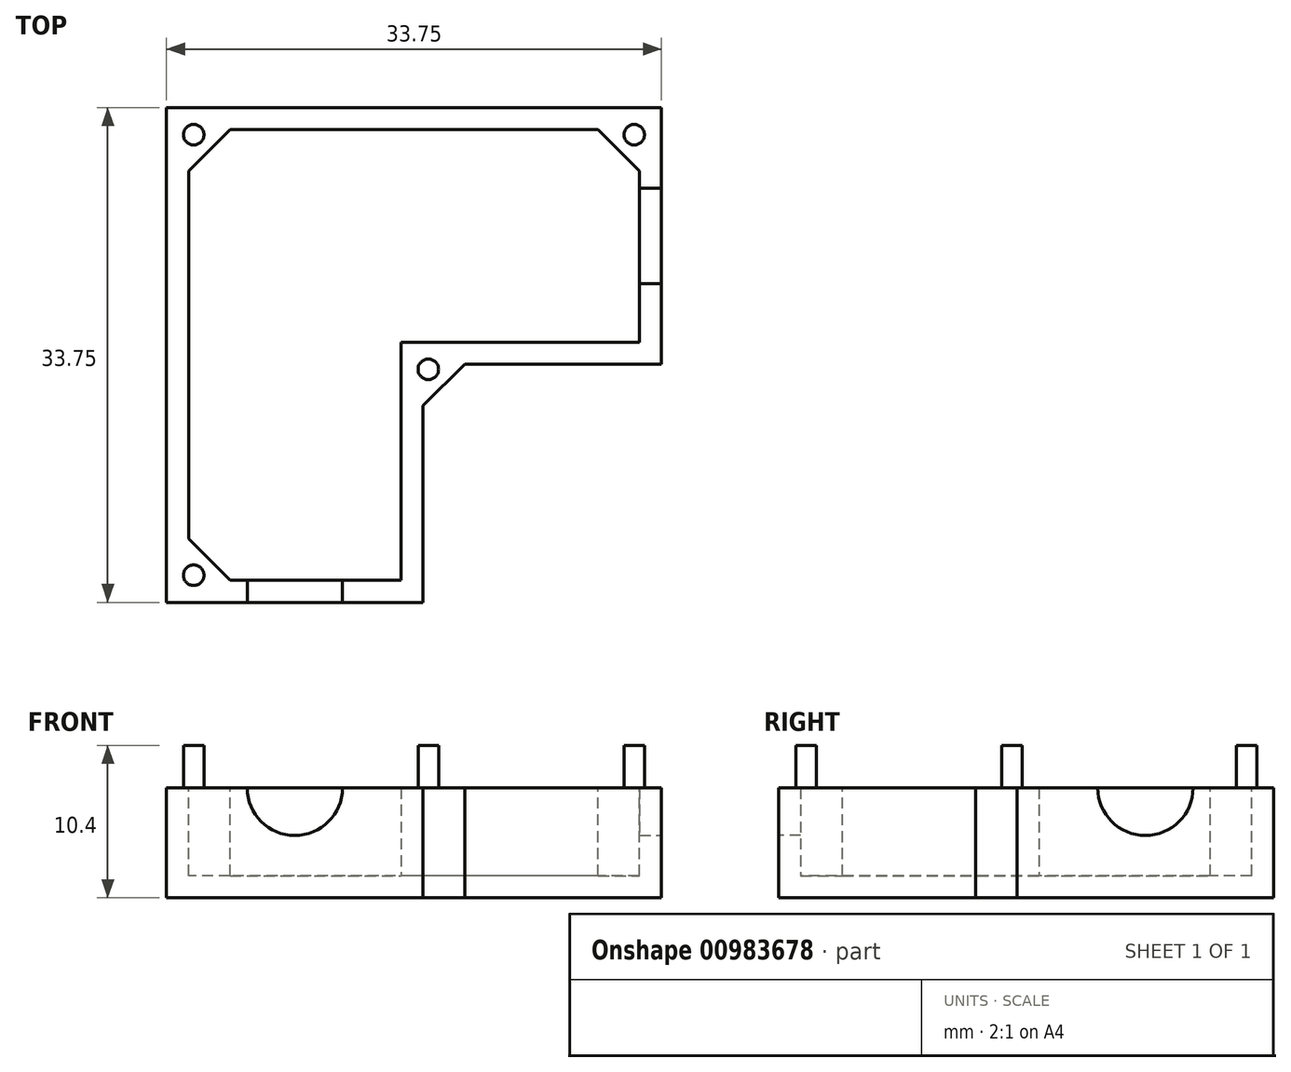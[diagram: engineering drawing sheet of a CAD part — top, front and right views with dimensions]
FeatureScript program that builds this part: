
annotation { "Feature Type Name" : "Feature", "Feature Type Description" : "" }
export const myFeature = defineFeature(function(context is Context, id is Id, definition is map)
    precondition{}
    {
        {
            var Q0;
            Q0=qCreatedBy(makeId("Top.planeOp"),FACE);
            var sketch = newSketch(context, id + "F0", { "sketchPlane" : qUnion([Q0])});
            skLineSegment(sketch, "E0.bottom", {"start": v(25, 8.75) * mm, "end": v(8.75, 8.75) * mm});
            skLineSegment(sketch, "E0.top", {"start": v(25, -8.75) * mm, "end": v(8.75, -8.75) * mm});
            skLineSegment(sketch, "E0.left", {"start": v(25, 8.75) * mm, "end": v(25, -8.75) * mm});
            skPoint(sketch, "E0.middle", {"position": v(0, 0) * mm});
            skLineSegment(sketch, "E1.top", {"start": v(-8.75, -25) * mm, "end": v(8.75, -25) * mm});
            skLineSegment(sketch, "E2.trimOffspring", {"start": v(-8.75, -8.75) * mm, "end": v(-8.75, -25) * mm});
            skLineSegment(sketch, "E3.trimOffspring", {"start": v(8.75, -8.75) * mm, "end": v(8.75, -25) * mm});
            skLineSegment(sketch, "E4", {"start": v(8.75, 8.75) * mm, "end": v(-8.75, 8.75) * mm});
            skLineSegment(sketch, "E5", {"start": v(-8.75, -8.75) * mm, "end": v(-8.75, 8.75) * mm});
            skLineSegment(sketch, "E6", {"start": v(0, 0) * mm, "end": v(0, -25) * mm});
            skLineSegment(sketch, "E7", {"start": v(0, 0) * mm, "end": v(25, 0) * mm});
            skLineSegment(sketch, "E8", {"start": v(0, 0) * mm, "end": v(-8.75, 0) * mm});
            skLineSegment(sketch, "E9", {"start": v(-8.75, 0) * mm, "end": v(0, 0) * mm});
            skLineSegment(sketch, "E10", {"start": v(0, 0) * mm, "end": v(0, 8.75) * mm});
            skSolve(sketch);
        }
        {
            var Q0;
            Q0=qSketchRegion(id+"F0",true);
            extrude(context, id + "F1", {"entities" : qUnion([Q0]), "depth" : 7.5 * mm, "offsetDistance" : 25 * mm});
        }
        {
            var Q0;
            Q0=makeQuery(id+"F1.opExtrude","CAP_FACE",FACE,{"disambiguationData":[OSD([sQuery(id+"F0.wireOp",EDGE,"E0.bottom"),sQuery(id+"F0.wireOp",EDGE,"E0.top"),sQuery(id+"F0.wireOp",EDGE,"E0.left"),sQuery(id+"F0.wireOp",EDGE,"E0.right"),sQuery(id+"F0.wireOp",EDGE,"E1.bottom"),sQuery(id+"F0.wireOp",EDGE,"E1.top"),sQuery(id+"F0.wireOp",EDGE,"E1.left"),sQuery(id+"F0.wireOp",EDGE,"E1.right"),sQuery(id+"F0.wireOp",EDGE,"1f207d6e-ecdf-4249-b46d-9234d2c6f181.trimOffspring"),sQuery(id+"F0.wireOp",EDGE,"E2.trimOffspring"),sQuery(id+"F0.wireOp",EDGE,"27587e5b-c096-4b03-bcea-66af693b9f10.trimOffspring"),sQuery(id+"F0.wireOp",EDGE,"E3.trimOffspring")])],"isStart":false});
            shell(context, id + "F2", {"entities" : qUnion([Q0]), "thickness" : 1.5 * mm});
        }
        {
            var Q0;
            Q0=makeQuery(id+"F1.opExtrude","CAP_FACE",FACE,{"disambiguationData":[OSD([sQuery(id+"F0.wireOp",EDGE,"E0.bottom"),sQuery(id+"F0.wireOp",EDGE,"E0.top"),sQuery(id+"F0.wireOp",EDGE,"E0.left"),sQuery(id+"F0.wireOp",EDGE,"E1.top"),sQuery(id+"F0.wireOp",EDGE,"E2.trimOffspring"),sQuery(id+"F0.wireOp",EDGE,"E3.trimOffspring"),sQuery(id+"F0.wireOp",EDGE,"E4"),sQuery(id+"F0.wireOp",EDGE,"E5")])],"isStart":false});
            var sketch = newSketch(context, id + "F3", { "sketchPlane" : qUnion([Q0])});
            skLineSegment(sketch, "E11", {"start": v(-7.25, 7.25) * mm, "end": v(-7.25, 4.42) * mm});
            skLineSegment(sketch, "E12", {"start": v(-7.25, 4.42) * mm, "end": v(-4.42, 7.25) * mm});
            skLineSegment(sketch, "E13", {"start": v(-4.42, 7.25) * mm, "end": v(-7.25, 7.25) * mm});
            skLineSegment(sketch, "E14", {"start": v(8.75, -8.75) * mm, "end": v(11.58, -8.75) * mm});
            skLineSegment(sketch, "E15", {"start": v(11.58, -8.75) * mm, "end": v(8.75, -11.58) * mm});
            skLineSegment(sketch, "E16", {"start": v(8.75, -11.58) * mm, "end": v(8.75, -8.75) * mm});
            skLineSegment(sketch, "E17", {"start": v(20.67, 7.25) * mm, "end": v(23.5, 4.42) * mm});
            skLineSegment(sketch, "E18", {"start": v(23.5, 4.42) * mm, "end": v(23.5, 7.25) * mm});
            skLineSegment(sketch, "E19", {"start": v(23.5, 7.25) * mm, "end": v(20.67, 7.25) * mm});
            skLineSegment(sketch, "E20", {"start": v(-7.25, -20.67) * mm, "end": v(-7.25, -23.5) * mm});
            skLineSegment(sketch, "E21", {"start": v(-7.25, -23.5) * mm, "end": v(-4.42, -23.5) * mm});
            skLineSegment(sketch, "E22", {"start": v(-4.42, -23.5) * mm, "end": v(-7.25, -20.67) * mm});
            skSolve(sketch);
        }
        {
            var Q0;
            Q0=qSketchRegion(id+"F3",true);
            var Q1;
            Q1=makeQuery(id+"F1.opExtrude","CAP_FACE",FACE,{"disambiguationData":[OSD([sQuery(id+"F0.wireOp",EDGE,"E0.bottom"),sQuery(id+"F0.wireOp",EDGE,"E0.top"),sQuery(id+"F0.wireOp",EDGE,"E0.left"),sQuery(id+"F0.wireOp",EDGE,"E1.top"),sQuery(id+"F0.wireOp",EDGE,"E2.trimOffspring"),sQuery(id+"F0.wireOp",EDGE,"E3.trimOffspring"),sQuery(id+"F0.wireOp",EDGE,"E4"),sQuery(id+"F0.wireOp",EDGE,"E5")])],"isStart":true});
            extrude(context, id + "F4", {"entities" : qUnion([Q0]), "operationType" : NewBodyOperationType.ADD, "endBound" : BoundingType.UP_TO_SURFACE, "oppositeDirection" : true, "depth" : 25 * mm, "endBoundEntityFace" : qUnion([Q1]), "offsetDistance" : 25 * mm});
        }
        {
            var Q0;
            Q0=makeQuery(id+"F4.boolean.opBoolean","MERGE",FACE,{"derivedFrom":[makeQuery(id+"F1.opExtrude","CAP_FACE",FACE,{"disambiguationData":[OSD([sQuery(id+"F0.wireOp",EDGE,"E0.bottom"),sQuery(id+"F0.wireOp",EDGE,"E0.top"),sQuery(id+"F0.wireOp",EDGE,"E0.left"),sQuery(id+"F0.wireOp",EDGE,"E1.top"),sQuery(id+"F0.wireOp",EDGE,"E2.trimOffspring"),sQuery(id+"F0.wireOp",EDGE,"E3.trimOffspring"),sQuery(id+"F0.wireOp",EDGE,"E4"),sQuery(id+"F0.wireOp",EDGE,"E5")])],"isStart":false}),makeQuery(id+"F4.opExtrude","CAP_FACE",FACE,{"disambiguationData":[OSD([sQuery(id+"F3.wireOp",EDGE,"E11"),sQuery(id+"F3.wireOp",EDGE,"E12"),sQuery(id+"F3.wireOp",EDGE,"E13")])],"isStart":true}),makeQuery(id+"F4.opExtrude","CAP_FACE",FACE,{"disambiguationData":[OSD([sQuery(id+"F3.wireOp",EDGE,"E14"),sQuery(id+"F3.wireOp",EDGE,"E15"),sQuery(id+"F3.wireOp",EDGE,"E16")])],"isStart":true}),makeQuery(id+"F4.opExtrude","CAP_FACE",FACE,{"disambiguationData":[OSD([sQuery(id+"F3.wireOp",EDGE,"E17"),sQuery(id+"F3.wireOp",EDGE,"E18"),sQuery(id+"F3.wireOp",EDGE,"E19")])],"isStart":true}),makeQuery(id+"F4.opExtrude","CAP_FACE",FACE,{"disambiguationData":[OSD([sQuery(id+"F3.wireOp",EDGE,"E20"),sQuery(id+"F3.wireOp",EDGE,"E21"),sQuery(id+"F3.wireOp",EDGE,"E22")])],"isStart":true})]});
            var sketch = newSketch(context, id + "F5", { "sketchPlane" : qUnion([Q0])});
            skCircle(sketch, "E23", {"center": v(-6.9, 6.9) * mm, "radius": 0.7 * mm});
            skCircle(sketch, "E24", {"center": v(23.15, 6.9) * mm, "radius": 0.7 * mm});
            skCircle(sketch, "E25", {"center": v(9.1, -9.1) * mm, "radius": 0.7 * mm});
            skCircle(sketch, "E26", {"center": v(-6.9, -23.15) * mm, "radius": 0.7 * mm});
            skLineSegment(sketch, "E27", {"start": v(-6.9, 6.9) * mm, "end": v(-5.84, 5.84) * mm});
            skLineSegment(sketch, "E28", {"start": v(23.15, 6.9) * mm, "end": v(22.09, 5.84) * mm});
            skLineSegment(sketch, "E29", {"start": v(9.1, -9.1) * mm, "end": v(10.16, -10.16) * mm});
            skLineSegment(sketch, "E30", {"start": v(-6.9, -23.15) * mm, "end": v(-5.84, -22.09) * mm});
            skSolve(sketch);
        }
        {
            var Q0;
            Q0=qSketchRegion(id+"F5",true);
            extrude(context, id + "F6", {"entities" : qUnion([Q0]), "operationType" : NewBodyOperationType.ADD, "depth" : 2.9 * mm, "offsetDistance" : 25 * mm});
        }
        {
            var Q0;
            Q0=makeQuery(id+"F1.opExtrude","SWEPT_FACE",FACE,{"disambiguationData":[OSD([sQuery(id+"F0.wireOp",EDGE,"E1.top")])]});
            var sketch = newSketch(context, id + "F7", { "sketchPlane" : qUnion([Q0])});
            skCircle(sketch, "E31", {"center": v(0, 7.5) * mm, "radius": 3.25 * mm});
            skSolve(sketch);
        }
        {
            var Q0;
            Q0=qSketchRegion(id+"F7",true);
            var Q1;
            Q1=makeQuery(id+"F2.opShell","OFFSET_FACE",FACE,{"disambiguationData":[OSD([sQuery(id+"F0.wireOp",EDGE,"E0.bottom"),sQuery(id+"F0.wireOp",EDGE,"E4")])]});
            extrude(context, id + "F8", {"entities" : qUnion([Q0]), "operationType" : NewBodyOperationType.REMOVE, "endBound" : BoundingType.UP_TO_SURFACE, "oppositeDirection" : true, "depth" : 25 * mm, "endBoundEntityFace" : qUnion([Q1]), "offsetDistance" : 25 * mm});
        }
        {
            var Q0;
            Q0=makeQuery(id+"F1.opExtrude","SWEPT_FACE",FACE,{"disambiguationData":[OSD([sQuery(id+"F0.wireOp",EDGE,"E0.left")])]});
            var sketch = newSketch(context, id + "F9", { "sketchPlane" : qUnion([Q0])});
            skCircle(sketch, "E32", {"center": v(0, 7.5) * mm, "radius": 3.25 * mm});
            skSolve(sketch);
        }
        {
            var Q0;
            Q0=qSketchRegion(id+"F9",true);
            var Q1;
            Q1=makeQuery(id+"F2.opShell","OFFSET_FACE",FACE,{"disambiguationData":[OSD([sQuery(id+"F0.wireOp",EDGE,"E2.trimOffspring"),sQuery(id+"F0.wireOp",EDGE,"E5")])]});
            extrude(context, id + "F10", {"entities" : qUnion([Q0]), "operationType" : NewBodyOperationType.REMOVE, "endBound" : BoundingType.UP_TO_SURFACE, "oppositeDirection" : true, "depth" : 25 * mm, "endBoundEntityFace" : qUnion([Q1]), "offsetDistance" : 25 * mm});
        }
    });
